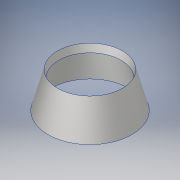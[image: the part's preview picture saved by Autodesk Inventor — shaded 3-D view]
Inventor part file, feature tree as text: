
AUTODESK INVENTOR PART (.ipt)
format: ipt  version: 2017 SP1 (Build 210196100, 196)  size: 135,168 bytes
history: native  units: in
note: dims shown in document units (in); Inventor stores cm internally (conversion verified against a paired STEP export)
features: revolve x1, sketch x1
ambient origin geometry x8: Origin, YZ Plane, XZ Plane, XY Plane, X Axis, Y Axis, Z Axis, Center Point
bodies: Body1 (feature_tree)
feature tree (2):
  revolve  "Revolution2"  [1 undecoded]
  sketch  "Sketch1"  dims[d0=1.13in d3=0.1718in d5=1.0in d6=1.0in d7=90.0deg d8=0.5in d9=15.0deg d31=0.25in d34=15.0deg d37=1.75in d38=4.5in d40=3.75in d41=0.125in d46=0.5in d47=0.5in d50=3.4in d51=0.5in d52=0.25in d53=90.0deg]
note: 1 required parameter value undecoded (feature->parameter linkage not recoverable at this tier; creation-order binding heuristic only, values carry confidence <= 0.55)
